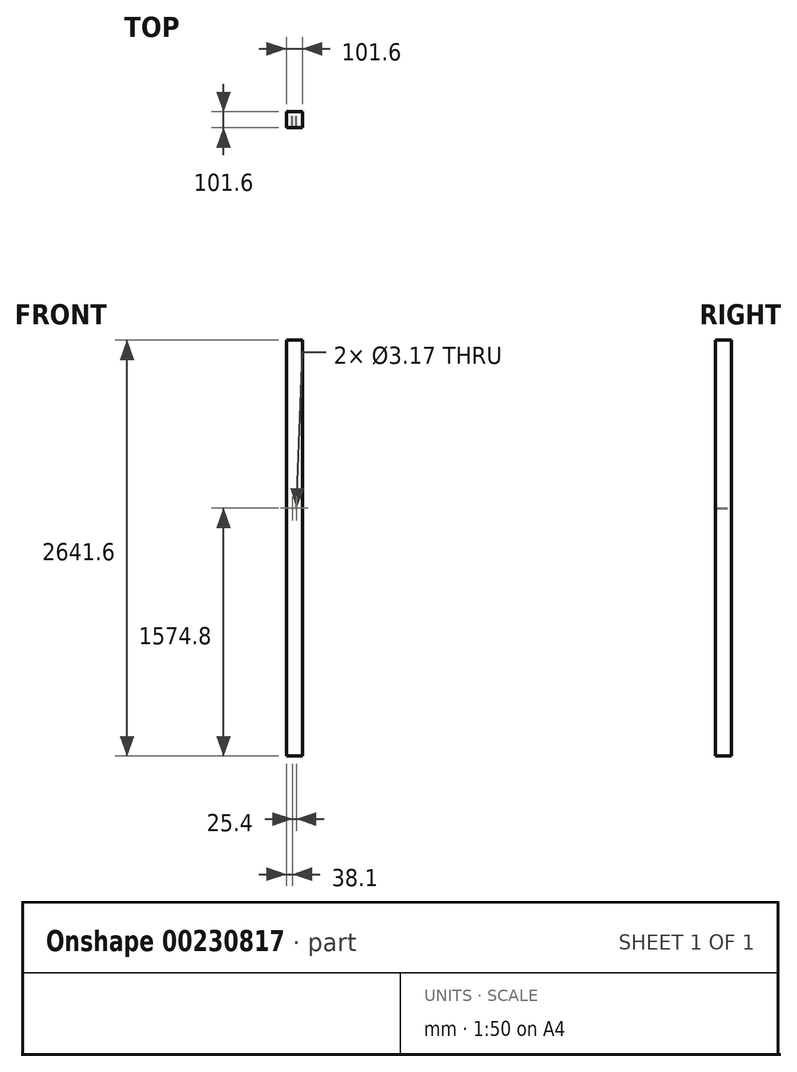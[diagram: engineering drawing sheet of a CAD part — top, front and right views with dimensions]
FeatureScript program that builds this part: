
annotation { "Feature Type Name" : "Feature", "Feature Type Description" : "" }
export const myFeature = defineFeature(function(context is Context, id is Id, definition is map)
    precondition{}
    {
        {
            var Q0;
            Q0=qCreatedBy(makeId("Front.planeOp"),FACE);
            var sketch = newSketch(context, id + "F0", { "sketchPlane" : qUnion([Q0])});
            skLineSegment(sketch, "E0.bottom", {"start": v(-49.9, 2456.66) * mm, "end": v(51.7, 2456.66) * mm});
            skLineSegment(sketch, "E0.top", {"start": v(-49.9, -184.94) * mm, "end": v(51.7, -184.94) * mm});
            skLineSegment(sketch, "E0.left", {"start": v(-49.9, 2456.66) * mm, "end": v(-49.9, -184.94) * mm});
            skLineSegment(sketch, "E0.right", {"start": v(51.7, 2456.66) * mm, "end": v(51.7, -184.94) * mm});
            skCircle(sketch, "E1", {"center": v(-11.8, 1389.86) * mm, "radius": 1.59 * mm});
            skCircle(sketch, "E2", {"center": v(13.6, 1389.86) * mm, "radius": 1.59 * mm});
            skSolve(sketch);
        }
        {
            var Q0;
            Q0=makeQuery(id+"F0.imprint","IMPRINT",FACE,{"disambiguationData":[TD([[makeQuery(id+"F0.imprint","IMPRINT",EDGE,{"derivedFrom":sQuery(id+"F0.wireOp",EDGE,"E0.bottom")}),-1.0]])]});
            extrude(context, id + "F1", {"entities" : qUnion([Q0]), "depth" : 101.6 * mm});
        }
    });
